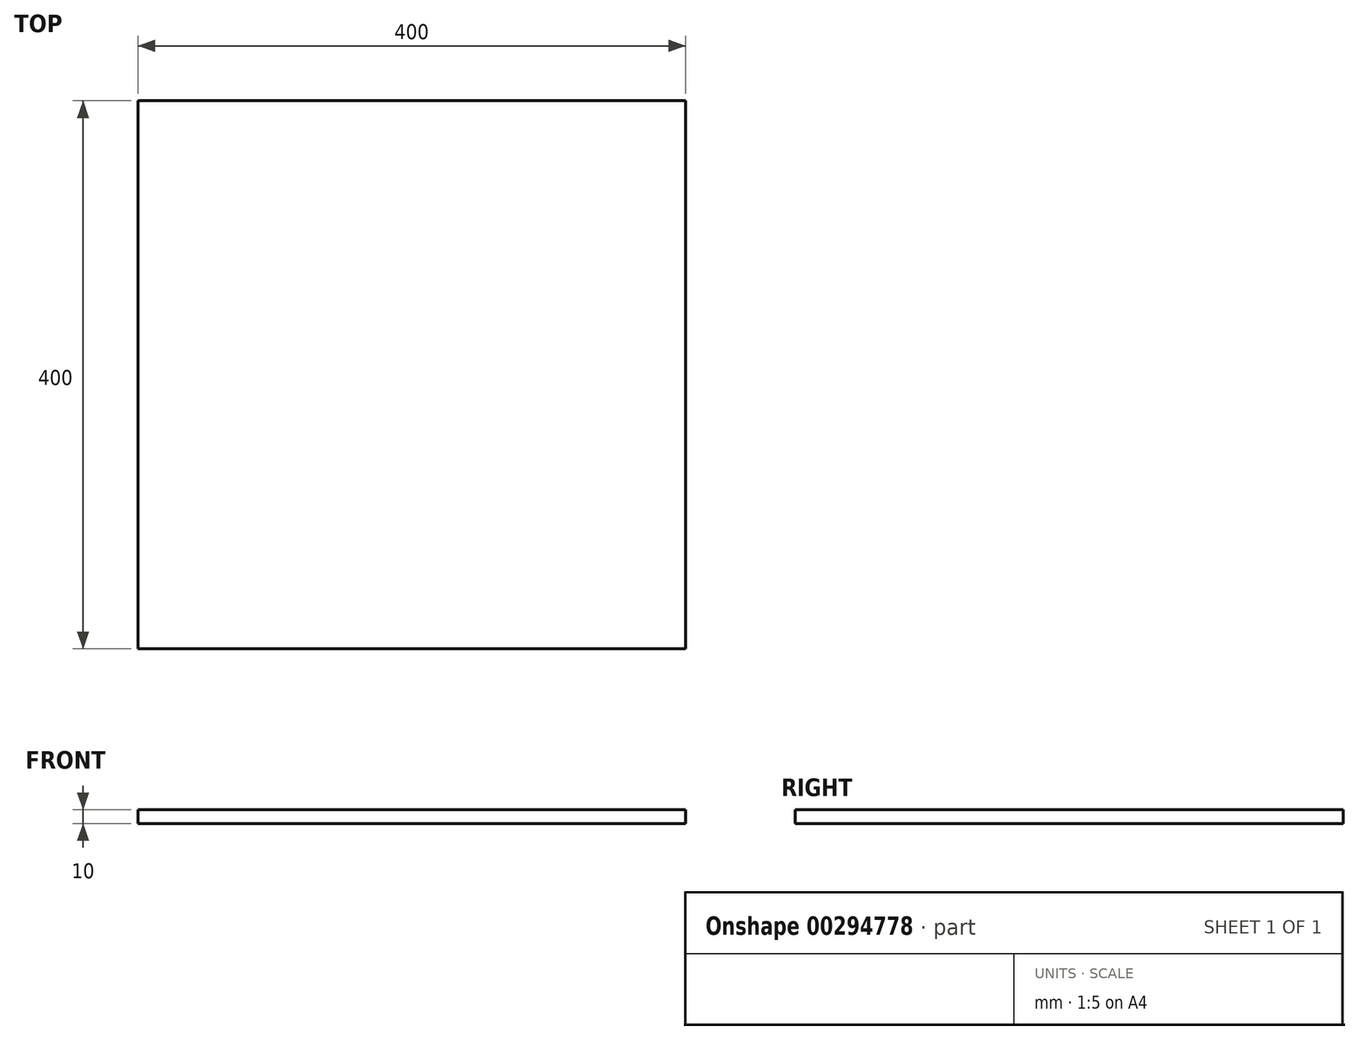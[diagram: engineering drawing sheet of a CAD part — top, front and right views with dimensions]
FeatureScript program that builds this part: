
annotation { "Feature Type Name" : "Feature", "Feature Type Description" : "" }
export const myFeature = defineFeature(function(context is Context, id is Id, definition is map)
    precondition{}
    {
        {
            var Q0;
            Q0=qCreatedBy(makeId("Top.planeOp"),FACE);
            var sketch = newSketch(context, id + "F0", { "sketchPlane" : qUnion([Q0])});
            skLineSegment(sketch, "E0.bottom", {"start": v(-200, 200) * mm, "end": v(200, 200) * mm});
            skLineSegment(sketch, "E0.top", {"start": v(-200, -200) * mm, "end": v(200, -200) * mm});
            skLineSegment(sketch, "E0.left", {"start": v(-200, 200) * mm, "end": v(-200, -200) * mm});
            skLineSegment(sketch, "E0.right", {"start": v(200, 200) * mm, "end": v(200, -200) * mm});
            skPoint(sketch, "E0.middle", {"position": v(0, 0) * mm});
            skSolve(sketch);
        }
        {
            var Q0;
            Q0=makeQuery(id+"F0.imprint","IMPRINT",FACE,{"disambiguationData":[TD([[makeQuery(id+"F0.imprint","IMPRINT",EDGE,{"derivedFrom":sQuery(id+"F0.wireOp",EDGE,"E0.bottom")}),-1.0]])]});
            extrude(context, id + "F1", {"entities" : qUnion([Q0]), "depth" : 10 * mm});
        }
    });
